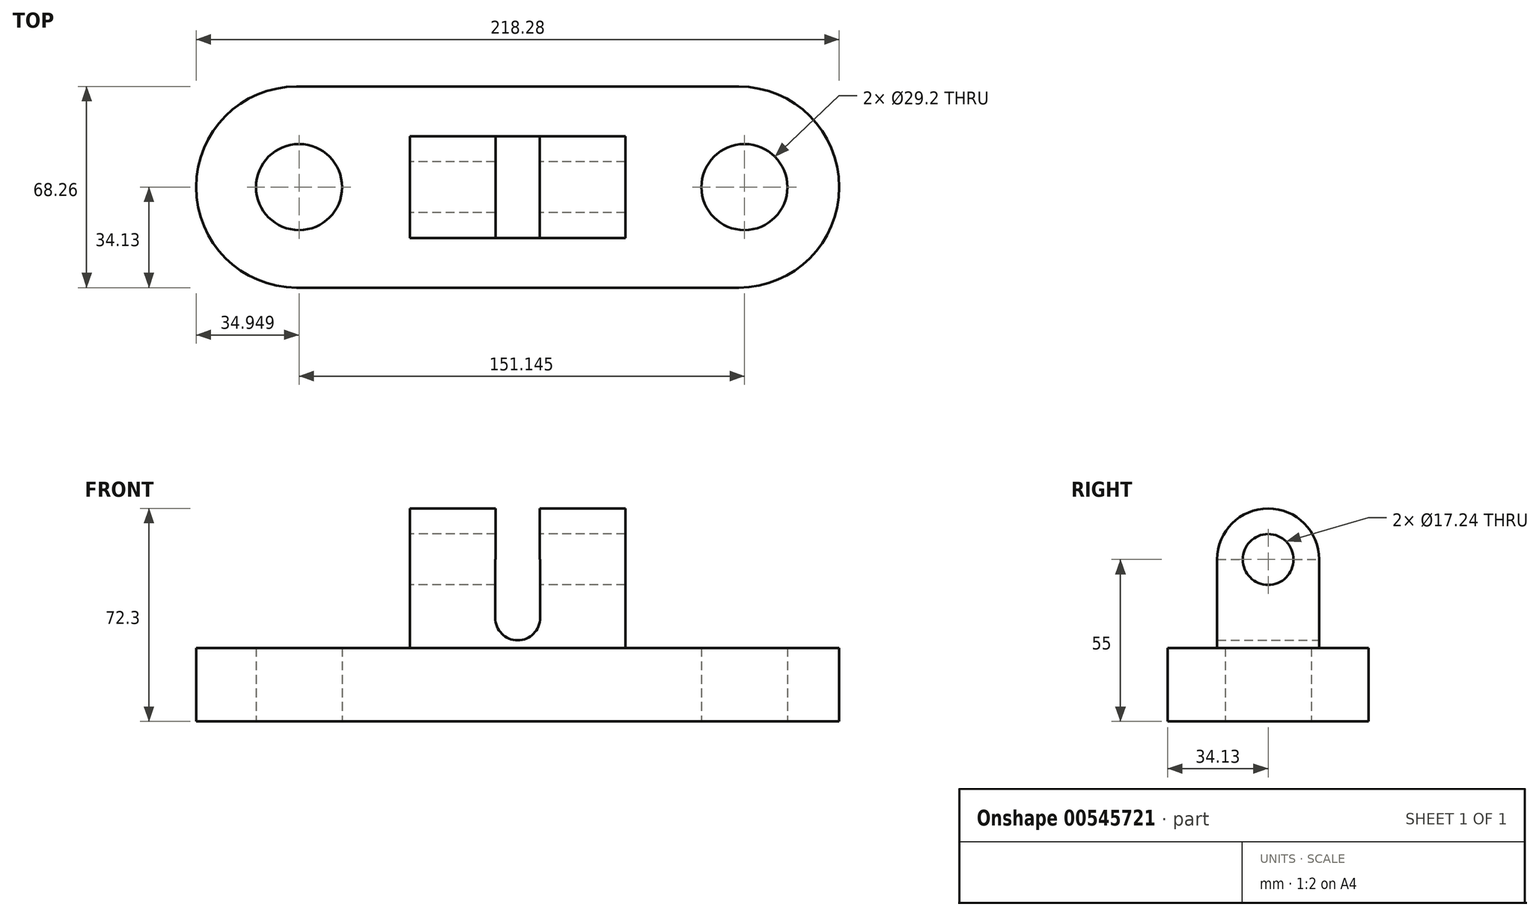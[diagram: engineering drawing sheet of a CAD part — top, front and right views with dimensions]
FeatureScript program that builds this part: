
annotation { "Feature Type Name" : "Feature", "Feature Type Description" : "" }
export const myFeature = defineFeature(function(context is Context, id is Id, definition is map)
    precondition{}
    {
        {
            var Q0;
            Q0=qCreatedBy(makeId("Top.planeOp"),FACE);
            var sketch = newSketch(context, id + "F0", { "sketchPlane" : qUnion([Q0])});
            skLineSegment(sketch, "E0.bottom", {"start": v(-75.02, 34.13) * mm, "end": v(75.02, 34.13) * mm});
            skLineSegment(sketch, "E0.top", {"start": v(-75.02, -34.13) * mm, "end": v(75.02, -34.13) * mm});
            skLineSegment(sketch, "E0.left", {"start": v(-75.02, 34.13) * mm, "end": v(-75.02, -34.13) * mm});
            skLineSegment(sketch, "E0.right", {"start": v(75.02, 34.13) * mm, "end": v(75.02, -34.13) * mm});
            skPoint(sketch, "E0.middle", {"position": v(0, 0) * mm});
            skArc(sketch, "E1", {"start": v(-75.02, 34.13) * mm, "mid": v(-109.14, 0) * mm, "end": v(-75.02, -34.13) * mm});
            skArc(sketch, "E2", {"start": v(75.02, -34.13) * mm, "mid": v(109.14, 0) * mm, "end": v(75.02, 34.13) * mm});
            skSolve(sketch);
        }
        {
            var Q0;
            Q0 = qSketchRegion(id + "F0", true);
            extrude(context, id + "F1", {"entities" : qUnion([Q0]), "depth" : 25 * mm, "offsetDistance" : 25 * mm});
        }
        {
            var Q0;
            Q0=qCreatedBy(makeId("Top.planeOp"),FACE);
            var sketch = newSketch(context, id + "F2", { "sketchPlane" : qUnion([Q0])});
            skCircle(sketch, "E3", {"center": v(-74.2, 0) * mm, "radius": 14.6 * mm});
            skCircle(sketch, "E4", {"center": v(76.95, 0) * mm, "radius": 14.6 * mm});
            skSolve(sketch);
        }
        {
            var Q0;
            Q0 = qSketchRegion(id + "F2", true);
            extrude(context, id + "F3", {"entities" : qUnion([Q0]), "operationType" : NewBodyOperationType.REMOVE, "depth" : 86 * mm, "offsetDistance" : 25 * mm});
        }
        {
            var Q0;
            Q0=makeQuery(id+"F1.opExtrude","CAP_FACE",FACE,{"disambiguationData":[OSD([sQuery(id+"F0.wireOp",EDGE,"E0.bottom"),sQuery(id+"F0.wireOp",EDGE,"E0.top"),sQuery(id+"F0.wireOp",EDGE,"E1"),sQuery(id+"F0.wireOp",EDGE,"E2")])],"isStart":false});
            var sketch = newSketch(context, id + "F4", { "sketchPlane" : qUnion([Q0])});
            skLineSegment(sketch, "E5.bottom", {"start": v(-36.53, -17.3) * mm, "end": v(36.53, -17.3) * mm});
            skLineSegment(sketch, "E5.top", {"start": v(-36.53, 17.3) * mm, "end": v(36.53, 17.3) * mm});
            skLineSegment(sketch, "E5.left", {"start": v(-36.53, -17.3) * mm, "end": v(-36.53, 17.3) * mm});
            skLineSegment(sketch, "E5.right", {"start": v(36.53, -17.3) * mm, "end": v(36.53, 17.3) * mm});
            skPoint(sketch, "E5.middle", {"position": v(0, 0) * mm});
            skSolve(sketch);
        }
        {
            var Q0;
            Q0=makeQuery(id+"F4.imprint","IMPRINT",FACE,{"disambiguationData":[TD([[makeQuery(id+"F4.imprint","IMPRINT",EDGE,{"derivedFrom":sQuery(id+"F4.wireOp",EDGE,"E5.bottom")}),1.0]])]});
            extrude(context, id + "F5", {"entities" : qUnion([Q0]), "operationType" : NewBodyOperationType.ADD, "depth" : 30 * mm, "offsetDistance" : 25 * mm});
        }
        {
            var Q0;
            Q0=makeQuery(id+"F5.opExtrude","SWEPT_FACE",FACE,{"disambiguationData":[OSD([sQuery(id+"F4.wireOp",EDGE,"E5.top")])]});
            var sketch = newSketch(context, id + "F6", { "sketchPlane" : qUnion([Q0])});
            skLineSegment(sketch, "E6.bottom", {"start": v(7.62, 35.2) * mm, "end": v(-7.62, 35.2) * mm});
            skLineSegment(sketch, "E6.left", {"start": v(7.62, 35.2) * mm, "end": v(7.62, 55) * mm});
            skLineSegment(sketch, "E6.right", {"start": v(-7.62, 35.2) * mm, "end": v(-7.62, 55) * mm});
            skPoint(sketch, "E6.middle", {"position": v(0, 55) * mm});
            skCircle(sketch, "E7", {"center": v(0, 35.2) * mm, "radius": 7.62 * mm});
            skPoint(sketch, "E8.orphan", {"position": v(-7.62, 74.8) * mm});
            skPoint(sketch, "E9.orphan", {"position": v(7.62, 74.8) * mm});
            skPoint(sketch, "E10.end.orphan", {"position": v(-14.93, 61.55) * mm});
            skPoint(sketch, "E11.end.orphan", {"position": v(17.7, 61.55) * mm});
            skSolve(sketch);
        }
        {
            var Q0;
            {var subQ0=sQuery(id+"F6.wireOp",EDGE,"E6.bottom");Q0=makeQuery(id+"F6.imprint","IMPRINT",FACE,{"disambiguationData":[TD([[makeQuery(id+"F6.imprint","IMPRINT",EDGE,{"derivedFrom":subQ0}),1.0]])]});}
            var Q1;
            {var subQ0=sQuery(id+"F6.wireOp",EDGE,"E6.bottom");Q1=makeQuery(id+"F6.imprint","IMPRINT",FACE,{"disambiguationData":[TD([[makeQuery(id+"F6.imprint","IMPRINT",EDGE,{"derivedFrom":subQ0}),-1.0]])]});}
            var Q2;
            {var subQ0=sQuery(id+"F6.wireOp",EDGE,"E6.top");Q2=makeQuery(id+"F6.imprint","IMPRINT",FACE,{"disambiguationData":[TD([[makeQuery(id+"F6.imprint","IMPRINT",EDGE,{"derivedFrom":subQ0}),1.0]])]});}
            var Q3;
            {var subQ1=sQuery(id+"F6.wireOp",EDGE,"E6.left");var subQ4=makeQuery(id+"F5.opExtrude","CAP_EDGE",EDGE,{"disambiguationData":[OSD([sQuery(id+"F4.wireOp",EDGE,"E5.top")])],"isStart":false});var subQ5=makeQuery(id+"F6.imprint","INTERSECT",VERTEX,{"derivedFrom":[subQ4,subQ1]});Q3=makeQuery(id+"F6.imprint","IMPRINT",FACE,{"disambiguationData":[TD([[makeQuery(id+"F6.imprint","IMPRINT",EDGE,{"disambiguationData":[TD([[subQ5,-1.0]])],"derivedFrom":subQ4}),1.0]])]});}
            extrude(context, id + "F7", {"entities" : qUnion([Q0, Q1, Q2, Q3]), "operationType" : NewBodyOperationType.REMOVE, "oppositeDirection" : true, "depth" : 50 * mm, "offsetDistance" : 25 * mm});
        }
        {
            var Q0;
            Q0=makeQuery(id+"F5.opExtrude","SWEPT_FACE",FACE,{"disambiguationData":[OSD([sQuery(id+"F4.wireOp",EDGE,"E5.right")])]});
            var sketch = newSketch(context, id + "F8", { "sketchPlane" : qUnion([Q0])});
            skArc(sketch, "E12", {"start": v(17.3, 55) * mm, "mid": v(0, 72.3) * mm, "end": v(-17.3, 55) * mm});
            skLineSegment(sketch, "E13", {"start": v(-17.3, 55) * mm, "end": v(17.3, 55) * mm});
            skSolve(sketch);
        }
        {
            var Q0;
            Q0 = qSketchRegion(id + "F8", true);
            extrude(context, id + "F9", {"entities" : qUnion([Q0]), "operationType" : NewBodyOperationType.ADD, "oppositeDirection" : true, "depth" : 29 * mm, "offsetDistance" : 25 * mm});
        }
        {
            var Q0;
            Q0=makeQuery(id+"F5.opExtrude","SWEPT_FACE",FACE,{"disambiguationData":[OSD([sQuery(id+"F4.wireOp",EDGE,"E5.left")])]});
            var sketch = newSketch(context, id + "F10", { "sketchPlane" : qUnion([Q0])});
            skArc(sketch, "E14", {"start": v(17.3, 55) * mm, "mid": v(0, 72.3) * mm, "end": v(-17.3, 55) * mm});
            skLineSegment(sketch, "E15", {"start": v(-17.3, 55) * mm, "end": v(17.3, 55) * mm});
            skSolve(sketch);
        }
        {
            var Q0;
            Q0 = qSketchRegion(id + "F10", true);
            extrude(context, id + "F11", {"entities" : qUnion([Q0]), "operationType" : NewBodyOperationType.ADD, "oppositeDirection" : true, "depth" : 29 * mm, "offsetDistance" : 25 * mm});
        }
        {
            var Q0;
            Q0=makeQuery(id+"F11.boolean.opBoolean","MERGE",FACE,{"derivedFrom":[makeQuery(id+"F5.opExtrude","SWEPT_FACE",FACE,{"disambiguationData":[OSD([sQuery(id+"F4.wireOp",EDGE,"E5.left")])]}),makeQuery(id+"F11.opExtrude","CAP_FACE",FACE,{"disambiguationData":[OSD([sQuery(id+"F10.wireOp",EDGE,"E14"),sQuery(id+"F10.wireOp",EDGE,"E15")])],"isStart":true})]});
            var sketch = newSketch(context, id + "F12", { "sketchPlane" : qUnion([Q0])});
            skCircle(sketch, "E16", {"center": v(0, 55) * mm, "radius": 8.62 * mm});
            skSolve(sketch);
        }
        {
            var Q0;
            Q0=makeQuery(id+"F12.imprint","IMPRINT",FACE,{"disambiguationData":[TD([[makeQuery(id+"F12.imprint","IMPRINT",EDGE,{"derivedFrom":sQuery(id+"F12.wireOp",EDGE,"E16")}),1.0]])]});
            extrude(context, id + "F13", {"entities" : qUnion([Q0]), "operationType" : NewBodyOperationType.REMOVE, "oppositeDirection" : true, "depth" : 110.5 * mm, "offsetDistance" : 25 * mm});
        }
    });
